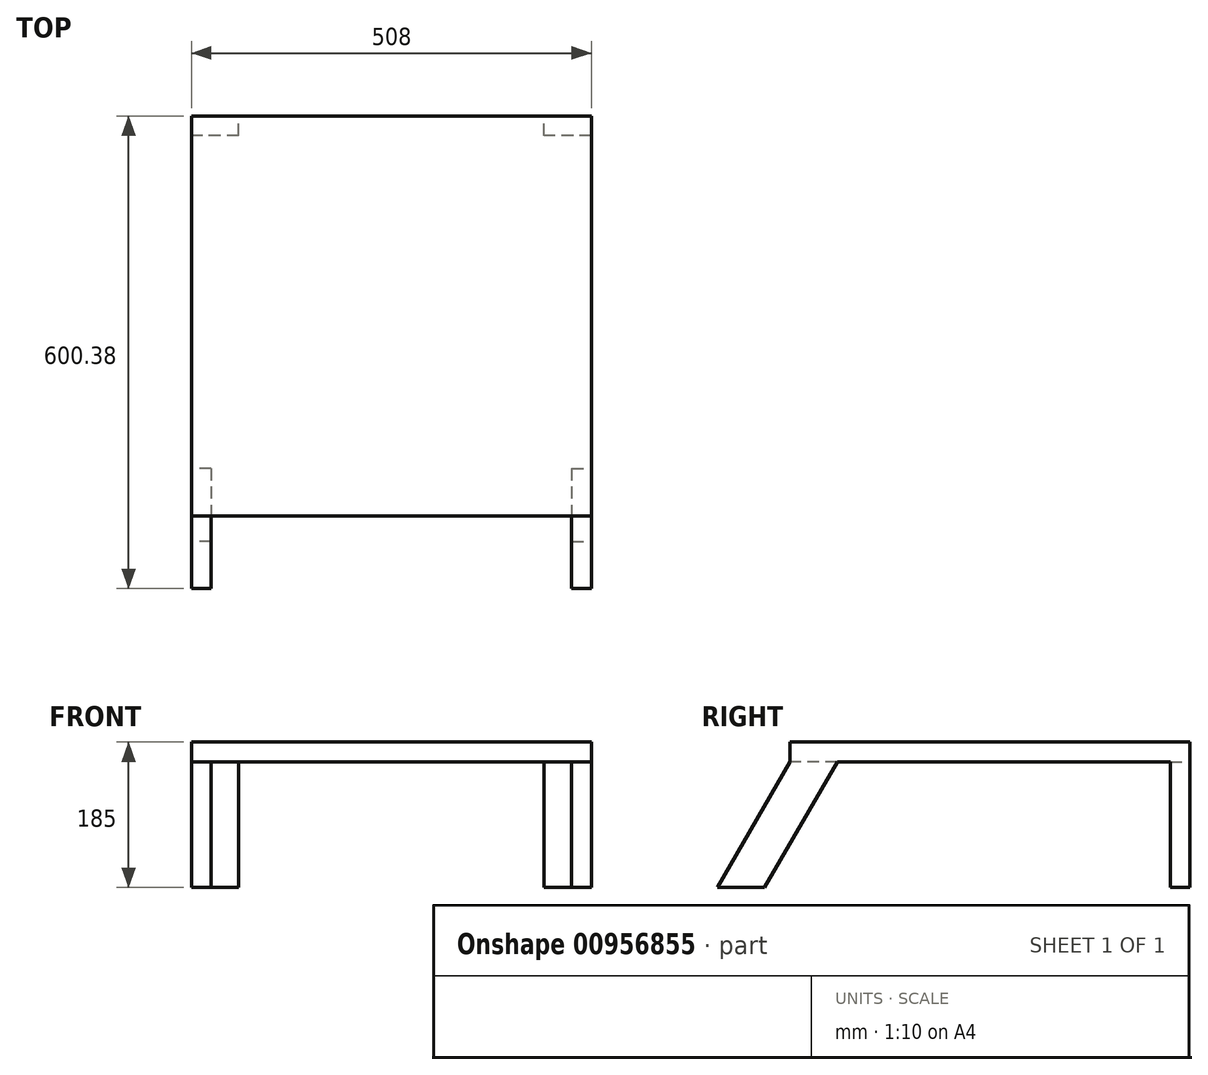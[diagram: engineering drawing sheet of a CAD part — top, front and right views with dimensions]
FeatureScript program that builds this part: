
annotation { "Feature Type Name" : "Feature", "Feature Type Description" : "" }
export const myFeature = defineFeature(function(context is Context, id is Id, definition is map)
    precondition{}
    {
        {
            var Q0;
            Q0=qCreatedBy(makeId("Top.planeOp"),FACE);
            var sketch = newSketch(context, id + "F0", { "sketchPlane" : qUnion([Q0])});
            skLineSegment(sketch, "E0.bottom", {"start": v(254, 254) * mm, "end": v(-254, 254) * mm});
            skLineSegment(sketch, "E0.top", {"start": v(254, -254) * mm, "end": v(-254, -254) * mm});
            skLineSegment(sketch, "E0.left", {"start": v(254, 254) * mm, "end": v(254, -254) * mm});
            skLineSegment(sketch, "E0.right", {"start": v(-254, 254) * mm, "end": v(-254, -254) * mm});
            skPoint(sketch, "E0.middle", {"position": v(0, 0) * mm});
            skSolve(sketch);
        }
        {
            var Q0;
            Q0 = qSketchRegion(id + "F0", true);
            extrude(context, id + "F1", {"entities" : qUnion([Q0]), "oppositeDirection" : true, "depth" : 25 * mm, "offsetDistance" : 25 * mm});
        }
        {
            var Q0;
            Q0=makeQuery(id+"F1.opExtrude","SWEPT_FACE",FACE,{"disambiguationData":[OSD([sQuery(id+"F0.wireOp",EDGE,"E0.right")])]});
            var sketch = newSketch(context, id + "F2", { "sketchPlane" : qUnion([Q0])});
            skLineSegment(sketch, "E1", {"start": v(194, -25) * mm, "end": v(286.38, -185) * mm});
            skLineSegment(sketch, "E2", {"start": v(286.38, -185) * mm, "end": v(286.38, -185) * mm});
            skLineSegment(sketch, "E3", {"start": v(346.38, -185) * mm, "end": v(286.38, -185) * mm});
            skLineSegment(sketch, "E4", {"start": v(346.38, -185) * mm, "end": v(254, -25) * mm});
            skLineSegment(sketch, "E5", {"start": v(254, -25) * mm, "end": v(254, -25) * mm});
            skLineSegment(sketch, "E6", {"start": v(254, -25) * mm, "end": v(194, -25) * mm});
            skSolve(sketch);
        }
        {
            var Q0;
            Q0 = qSketchRegion(id + "F2", true);
            extrude(context, id + "F3", {"entities" : qUnion([Q0]), "oppositeDirection" : true, "depth" : 25 * mm, "offsetDistance" : 25 * mm});
        }
        {
            var Q0;
            Q0=makeQuery(id+"F3.opExtrude","SWEPT_BODY",BODY,{"disambiguationData":[OSD([sQuery(id+"F2.wireOp",EDGE,"E1"),sQuery(id+"F2.wireOp",EDGE,"E3"),sQuery(id+"F2.wireOp",EDGE,"E4"),sQuery(id+"F2.wireOp",EDGE,"E6")])]});
            var Q1;
            Q1=qCreatedBy(makeId("Right.planeOp"),FACE);
            mirror(context, id + "F4", {"operationType" : NewBodyOperationType.ADD, "entities" : qUnion([Q0]), "mirrorPlane" : qUnion([Q1])});
        }
        {
            var Q0;
            Q0=makeQuery(id+"F1.opExtrude","SWEPT_FACE",FACE,{"disambiguationData":[OSD([sQuery(id+"F0.wireOp",EDGE,"E0.bottom")])]});
            var sketch = newSketch(context, id + "F5", { "sketchPlane" : qUnion([Q0])});
            skLineSegment(sketch, "E7.bottom", {"start": v(-254, -25) * mm, "end": v(-194, -25) * mm});
            skLineSegment(sketch, "E7.top", {"start": v(-254, -185) * mm, "end": v(-194, -185) * mm});
            skLineSegment(sketch, "E7.left", {"start": v(-254, -25) * mm, "end": v(-254, -185) * mm});
            skLineSegment(sketch, "E7.right", {"start": v(-194, -25) * mm, "end": v(-194, -185) * mm});
            skLineSegment(sketch, "E8", {"start": v(0, 0) * mm, "end": v(0, -195.2) * mm, "construction": true});
            skLineSegment(sketch, "E9.MirrorCS", {"start": v(254, -185) * mm, "end": v(194, -185) * mm});
            skLineSegment(sketch, "E10.MirrorCS", {"start": v(194, -25) * mm, "end": v(194, -185) * mm});
            skLineSegment(sketch, "E11.MirrorCS", {"start": v(254, -25) * mm, "end": v(194, -25) * mm});
            skLineSegment(sketch, "E12.MirrorCS", {"start": v(254, -25) * mm, "end": v(254, -185) * mm});
            skSolve(sketch);
        }
        {
            var Q0;
            Q0 = qSketchRegion(id + "F5", true);
            extrude(context, id + "F6", {"entities" : qUnion([Q0]), "operationType" : NewBodyOperationType.ADD, "oppositeDirection" : true, "depth" : 25 * mm, "offsetDistance" : 25 * mm});
        }
    });
